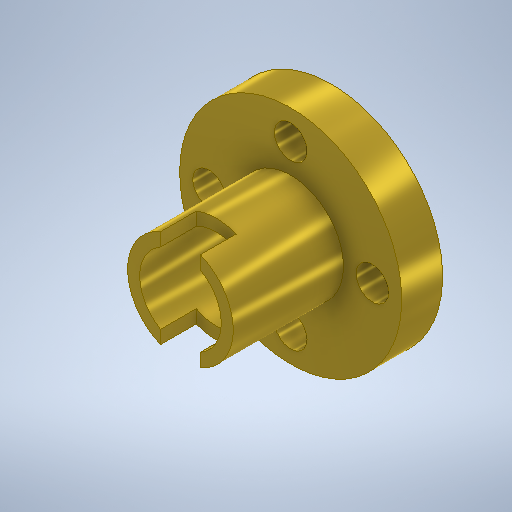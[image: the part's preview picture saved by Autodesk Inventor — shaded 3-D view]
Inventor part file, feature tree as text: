
AUTODESK INVENTOR PART (.ipt)
format: ipt  version: 2025.2 (Build 292293000, 293)  size: 303,616 bytes
history: native  units: mm
features: sketch x6, extrude x3, other x1, hole x1, projected_geometry x1
ambient origin geometry x8: Origin, YZ Plane, XZ Plane, XY Plane, X Axis, Y Axis, Z Axis, Center Point
bodies: Body1 (feature_tree)
feature tree (12):
  other  "Bryła1"
  extrude  "Wyciągnięcie proste1"  Depth=8.0mm
  hole  "Otwór1"  [1 undecoded]
  extrude  "Wyciągnięcie proste2"  Depth=4.0mm TaperAngle=0.0deg
  extrude  "Wyciągnięcie proste3"  Depth=3.9mm TaperAngle=360.0deg
  sketch  "Szkic1"
  sketch  "Sketch Circular Pattern1"  dims[d0=21.75mm d1=8.0mm]
  sketch  "Szkic2"
  projected_geometry  "Pętla rzutowana1"
  sketch  "Sketch Circular Pattern2"  dims[d2=8.0mm d3=40.0mm d5=360.0deg d7=4.0mm d8=0.0mm d9=40.0mm d11=360.0deg d13=3.2mm d14=6.0mm d15=4.0mm d16=2.0mm d17=90.0deg d18=8.0mm d19=20.594885mm d20=8.0mm d21=10.34mm d22=10.8mm d23=0.0mm d24=10.34mm d25=7.3mm d26=10.34mm d27=3.9mm d28=0.0mm]
  sketch  "Szkic3"
  sketch  "Szkic4"
note: 1 required parameter value undecoded (feature->parameter linkage not recoverable at this tier; creation-order binding heuristic only, values carry confidence <= 0.55)
